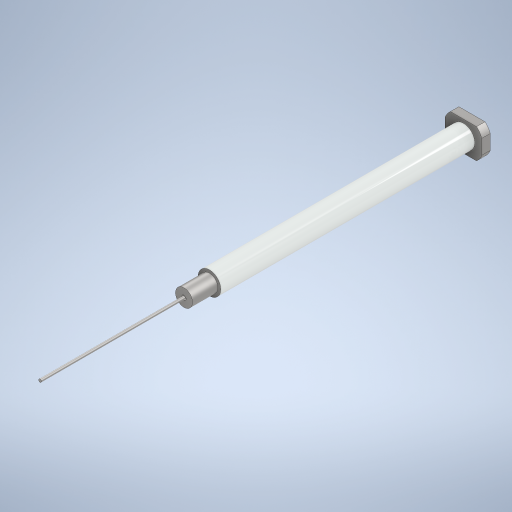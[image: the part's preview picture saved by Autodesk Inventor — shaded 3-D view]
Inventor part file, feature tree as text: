
AUTODESK INVENTOR PART (.ipt)
format: ipt  version: 2023.2 (Build 272271000, 271)  size: 286,720 bytes
history: native  units: mm
features: extrude x6, sketch x5
ambient origin geometry x8: Origin, YZ Plane, XZ Plane, XY Plane, X Axis, Y Axis, Z Axis, Center Point
bodies: Solid1 (feature_tree)
feature tree (11):
  extrude  "Extrusion1"  Depth=99.0mm TaperAngle=0.0deg
  extrude  "Extrusion2"  Depth=9.0mm TaperAngle=0.0deg
  extrude  "Extrusion3"  TaperAngle=0.0deg  [1 undecoded]
  extrude  "Extrusion4"  Depth=51.0mm TaperAngle=0.0deg
  sketch  "Sketch6"  dims[d12=13.0mm d13=10.5mm d14=3.0mm d15=0.0mm d16=14.0mm d17=3.0mm d18=0.0mm]
  extrude  "Extrusion5"  Depth=10.5mm
  extrude  "Extrusion6"  Depth=3.0mm TaperAngle=0.0deg
  sketch  "Sketch1"  dims[d0=8.0mm d1=99.0mm d2=0.0mm]
  sketch  "Sketch2"  dims[d3=6.0mm d4=9.0mm d5=0.0mm]
  sketch  "Sketch3"  dims[d6=1.5mm d7=0.0mm d8=0.0mm]
  sketch  "Sketch5"  dims[d9=1.0mm d10=51.0mm d11=0.0mm]
note: 1 required parameter value undecoded (feature->parameter linkage not recoverable at this tier; creation-order binding heuristic only, values carry confidence <= 0.55)
